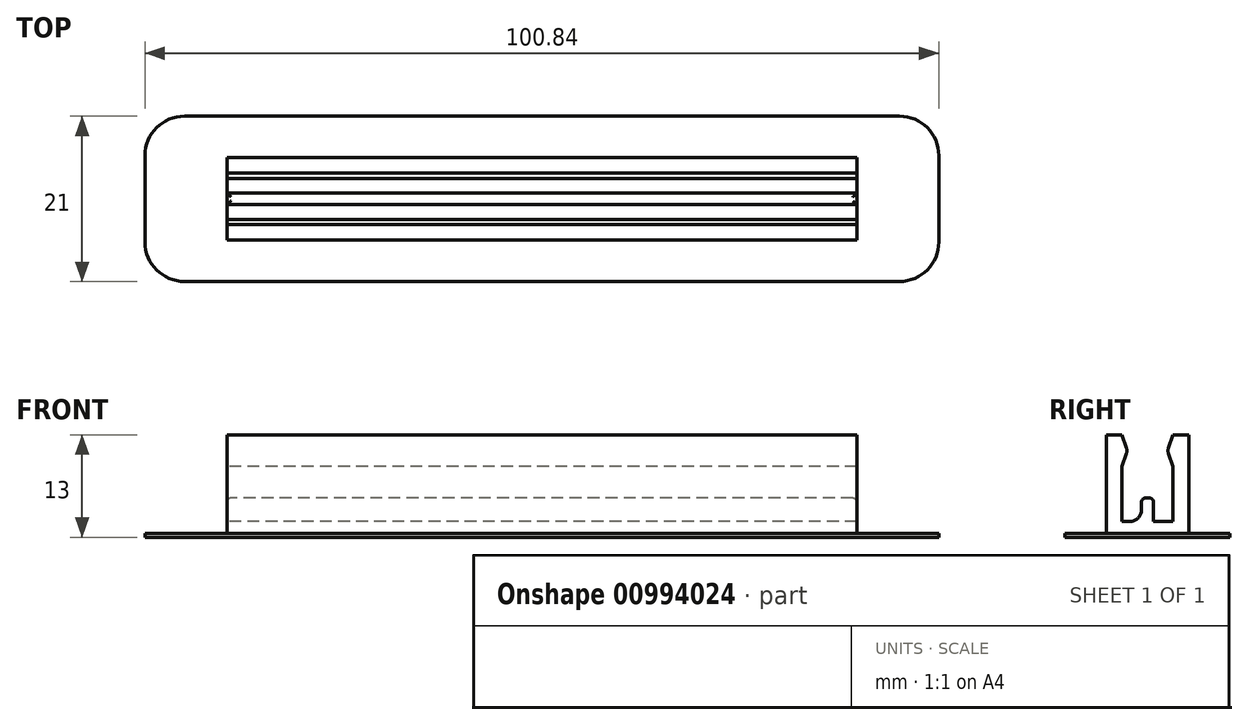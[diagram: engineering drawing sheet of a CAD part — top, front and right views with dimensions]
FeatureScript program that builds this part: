
annotation { "Feature Type Name" : "Feature", "Feature Type Description" : "" }
export const myFeature = defineFeature(function(context is Context, id is Id, definition is map)
    precondition{}
    {
        {
            var Q0;
            Q0=qCreatedBy(makeId("Top.planeOp"),FACE);
            var sketch = newSketch(context, id + "F0", { "sketchPlane" : qUnion([Q0])});
            skLineSegment(sketch, "E0.bottom", {"start": v(40, 5.25) * mm, "end": v(-40, 5.25) * mm});
            skLineSegment(sketch, "E0.top", {"start": v(40, -5.25) * mm, "end": v(-40, -5.25) * mm});
            skLineSegment(sketch, "E0.left", {"start": v(40, 5.25) * mm, "end": v(40, -5.25) * mm});
            skLineSegment(sketch, "E0.right", {"start": v(-40, 5.25) * mm, "end": v(-40, -5.25) * mm});
            skPoint(sketch, "E0.middle", {"position": v(0, 0) * mm});
            skLineSegment(sketch, "E1.bottom", {"start": v(-40, 5.25) * mm, "end": v(40, 5.25) * mm});
            skLineSegment(sketch, "E1.top", {"start": v(-40, 3.25) * mm, "end": v(40, 3.25) * mm});
            skLineSegment(sketch, "E1.left", {"start": v(-40, 5.25) * mm, "end": v(-40, 3.25) * mm});
            skLineSegment(sketch, "E1.right", {"start": v(40, 5.25) * mm, "end": v(40, 3.25) * mm});
            skLineSegment(sketch, "E2.bottom", {"start": v(-40, -5.25) * mm, "end": v(40, -5.25) * mm});
            skLineSegment(sketch, "E2.top", {"start": v(-40, -3.25) * mm, "end": v(40, -3.25) * mm});
            skLineSegment(sketch, "E2.left", {"start": v(-40, -5.25) * mm, "end": v(-40, -3.25) * mm});
            skLineSegment(sketch, "E2.right", {"start": v(40, -5.25) * mm, "end": v(40, -3.25) * mm});
            skLineSegment(sketch, "E3.bottom", {"start": v(45.42, 10.5) * mm, "end": v(-45.42, 10.5) * mm});
            skLineSegment(sketch, "E3.top", {"start": v(45.42, -10.5) * mm, "end": v(-45.42, -10.5) * mm});
            skLineSegment(sketch, "E3.left", {"start": v(50.42, 5.5) * mm, "end": v(50.42, -5.5) * mm});
            skLineSegment(sketch, "E3.right", {"start": v(-50.42, 5.5) * mm, "end": v(-50.42, -5.5) * mm});
            skPoint(sketch, "E4.visualSharp", {"position": v(-50.42, 10.5) * mm});
            skArc(sketch, "E4.filletArc", {"start": v(-45.42, 10.5) * mm, "mid": v(-48.95, 9.03) * mm, "end": v(-50.42, 5.5) * mm});
            skPoint(sketch, "E5.visualSharp", {"position": v(-50.42, -10.5) * mm});
            skArc(sketch, "E5.filletArc", {"start": v(-50.42, -5.5) * mm, "mid": v(-48.95, -9.03) * mm, "end": v(-45.42, -10.5) * mm});
            skPoint(sketch, "E6.visualSharp", {"position": v(50.42, 10.5) * mm});
            skArc(sketch, "E6.filletArc", {"start": v(50.42, 5.5) * mm, "mid": v(48.95, 9.03) * mm, "end": v(45.42, 10.5) * mm});
            skPoint(sketch, "E7.visualSharp", {"position": v(50.42, -10.5) * mm});
            skArc(sketch, "E7.filletArc", {"start": v(45.42, -10.5) * mm, "mid": v(48.95, -9.03) * mm, "end": v(50.42, -5.5) * mm});
            skSolve(sketch);
        }
        {
            var Q0;
            {var subQ0=sQuery(id+"F0.wireOp",EDGE,"E1.top");Q0=makeQuery(id+"F0.imprint","IMPRINT",FACE,{"disambiguationData":[TD([[makeQuery(id+"F0.imprint","IMPRINT",EDGE,{"derivedFrom":subQ0}),-1.0]])]});}
            extrude(context, id + "F1", {"entities" : qUnion([Q0]), "depth" : 2 * mm, "offsetDistance" : 25 * mm});
        }
        {
            var Q0;
            {var subQ0=sQuery(id+"F0.wireOp",EDGE,"E0.bottom");Q0=makeQuery(id+"F0.imprint","IMPRINT",FACE,{"disambiguationData":[TD([[makeQuery(id+"F0.imprint","IMPRINT",EDGE,{"derivedFrom":subQ0}),1.0]])]});}
            var Q1;
            {var subQ0=sQuery(id+"F0.wireOp",EDGE,"E0.top");Q1=makeQuery(id+"F0.imprint","IMPRINT",FACE,{"disambiguationData":[TD([[makeQuery(id+"F0.imprint","IMPRINT",EDGE,{"derivedFrom":subQ0}),-1.0]])]});}
            extrude(context, id + "F2", {"entities" : qUnion([Q0, Q1]), "operationType" : NewBodyOperationType.ADD, "depth" : 13 * mm, "offsetDistance" : 25 * mm});
        }
        {
            var Q0;
            {var subQ0=sQuery(id+"F0.wireOp",EDGE,"E0.right");Q0=makeQuery(id+"F2.boolean.opBoolean","MERGE",FACE,{"derivedFrom":[makeQuery(id+"F1.opExtrude","SWEPT_FACE",FACE,{"disambiguationData":[OSD([subQ0])]}),makeQuery(id+"F2.opExtrude","SWEPT_FACE",FACE,{"disambiguationData":[OSD([subQ0]),TDD([makeQuery(id+"F0.imprint","IMPRINT",EDGE,{"disambiguationData":[TD([[makeQuery(id+"F0.imprint","INTERSECT",VERTEX,{"derivedFrom":[sQuery(id+"F0.wireOp",EDGE,"E0.bottom"),subQ0]}),-1.0]])],"derivedFrom":subQ0})])]}),makeQuery(id+"F2.opExtrude","SWEPT_FACE",FACE,{"disambiguationData":[OSD([subQ0]),TDD([makeQuery(id+"F0.imprint","IMPRINT",EDGE,{"disambiguationData":[TD([[makeQuery(id+"F0.imprint","INTERSECT",VERTEX,{"derivedFrom":[sQuery(id+"F0.wireOp",EDGE,"E0.top"),subQ0]}),1.0]])],"derivedFrom":subQ0})])]})]});}
            var sketch = newSketch(context, id + "F3", { "sketchPlane" : qUnion([Q0])});
            skLineSegment(sketch, "E8.bottom", {"start": v(-5.25, 13) * mm, "end": v(5.25, 13) * mm, "construction": true});
            skLineSegment(sketch, "E8.top", {"start": v(-5.25, 9) * mm, "end": v(5.25, 9) * mm, "construction": true});
            skLineSegment(sketch, "E8.left", {"start": v(-5.25, 13) * mm, "end": v(-5.25, 9) * mm, "construction": true});
            skLineSegment(sketch, "E8.right", {"start": v(5.25, 13) * mm, "end": v(5.25, 9) * mm, "construction": true});
            skLineSegment(sketch, "E9.bottom", {"start": v(-3.25, 13) * mm, "end": v(-2.55, 13) * mm, "construction": true});
            skLineSegment(sketch, "E9.top", {"start": v(-3.25, 9) * mm, "end": v(-2.55, 9) * mm, "construction": true});
            skLineSegment(sketch, "E9.left", {"start": v(-3.25, 13) * mm, "end": v(-3.25, 9) * mm, "construction": true});
            skLineSegment(sketch, "E9.right", {"start": v(-2.55, 13) * mm, "end": v(-2.55, 9) * mm, "construction": true});
            skLineSegment(sketch, "E10.top", {"start": v(3.25, 13) * mm, "end": v(3.05, 13) * mm, "construction": true});
            skLineSegment(sketch, "E10.left", {"start": v(3.25, 7.5) * mm, "end": v(3.25, 13) * mm, "construction": true});
            skLineSegment(sketch, "E11.bottom", {"start": v(-3.25, 13) * mm, "end": v(3.25, 13) * mm, "construction": true});
            skLineSegment(sketch, "E11.left", {"start": v(-3.25, 13) * mm, "end": v(-3.25, 10.25) * mm, "construction": true});
            skLineSegment(sketch, "E11.right", {"start": v(3.25, 13) * mm, "end": v(3.25, 10.25) * mm, "construction": true});
            skLineSegment(sketch, "E12", {"start": v(-3.25, 9) * mm, "end": v(-2.55, 11) * mm});
            skLineSegment(sketch, "E13", {"start": v(-2.55, 11) * mm, "end": v(-3.25, 13) * mm});
            skLineSegment(sketch, "E14.top", {"start": v(-3.25, 11) * mm, "end": v(3.25, 11) * mm, "construction": true});
            skLineSegment(sketch, "E14.left", {"start": v(-3.25, 13) * mm, "end": v(-3.25, 11) * mm, "construction": true});
            skLineSegment(sketch, "E14.right", {"start": v(3.25, 13) * mm, "end": v(3.25, 11) * mm, "construction": true});
            skLineSegment(sketch, "E15.bottom", {"start": v(3.25, 13) * mm, "end": v(2.55, 13) * mm, "construction": true});
            skLineSegment(sketch, "E15.top", {"start": v(3.25, 9) * mm, "end": v(2.55, 9) * mm, "construction": true});
            skLineSegment(sketch, "E15.left", {"start": v(3.25, 13) * mm, "end": v(3.25, 9) * mm, "construction": true});
            skLineSegment(sketch, "E15.right", {"start": v(2.55, 13) * mm, "end": v(2.55, 9) * mm, "construction": true});
            skLineSegment(sketch, "E16", {"start": v(3.25, 9) * mm, "end": v(2.55, 11) * mm});
            skLineSegment(sketch, "E17", {"start": v(2.55, 11) * mm, "end": v(3.25, 13) * mm});
            skLineSegment(sketch, "E18.bottom", {"start": v(-0.75, 2) * mm, "end": v(0.75, 2) * mm});
            skLineSegment(sketch, "E18.top", {"start": v(-0.75, 5) * mm, "end": v(0.75, 5) * mm});
            skLineSegment(sketch, "E18.left", {"start": v(-0.75, 2) * mm, "end": v(-0.75, 5) * mm});
            skLineSegment(sketch, "E18.right", {"start": v(0.75, 2) * mm, "end": v(0.75, 5) * mm});
            skSolve(sketch);
        }
        {
            var Q0;
            {var subQ0=sQuery(id+"F3.wireOp",EDGE,"E12");Q0=makeQuery(id+"F3.imprint","IMPRINT",FACE,{"disambiguationData":[TD([[makeQuery(id+"F3.imprint","IMPRINT",EDGE,{"derivedFrom":subQ0}),1.0]])]});}
            var Q1;
            {var subQ0=sQuery(id+"F3.wireOp",EDGE,"JF0y7yOE-hZ0c-IGpq-qxWO-KcFmzZiD7cJA");Q1=makeQuery(id+"F3.imprint","IMPRINT",FACE,{"disambiguationData":[TD([[makeQuery(id+"F3.imprint","IMPRINT",EDGE,{"derivedFrom":subQ0}),-1.0]])]});}
            var Q2;
            {var subQ0=sQuery(id+"F3.wireOp",EDGE,"E16");Q2=makeQuery(id+"F3.imprint","IMPRINT",FACE,{"disambiguationData":[TD([[makeQuery(id+"F3.imprint","IMPRINT",EDGE,{"derivedFrom":subQ0}),-1.0]])]});}
            var Q3;
            Q3=makeQuery(id+"F3.imprint","IMPRINT",FACE,{"disambiguationData":[TD([[makeQuery(id+"F3.imprint","IMPRINT",EDGE,{"derivedFrom":sQuery(id+"F3.wireOp",EDGE,"E18.bottom")}),1.0]])]});
            extrude(context, id + "F4", {"entities" : qUnion([Q0, Q1, Q2, Q3]), "operationType" : NewBodyOperationType.ADD, "depth" : -80 * mm, "offsetDistance" : 25 * mm});
        }
        {
            var Q0;
            Q0=makeQuery(id+"F4.opExtrude","SWEPT_EDGE",EDGE,{"disambiguationData":[OSD([sQuery(id+"F3.wireOp",EDGE,"E12"),sQuery(id+"F3.wireOp",EDGE,"E13")])]});
            fillet(context, id + "F5", {"entities" : qUnion([Q0]), "radius" : 1 * mm, "tangentPropagation" : true, "allowEdgeOverflow" : false});
        }
        {
            var Q0;
            Q0=makeQuery(id+"F4.opExtrude","SWEPT_EDGE",EDGE,{"disambiguationData":[OSD([sQuery(id+"F3.wireOp",EDGE,"E16"),sQuery(id+"F3.wireOp",EDGE,"E17")])]});
            fillet(context, id + "F6", {"entities" : qUnion([Q0]), "radius" : 1 * mm, "tangentPropagation" : true, "allowEdgeOverflow" : false});
        }
        {
            var Q0;
            Q0=makeQuery(id+"F1.opExtrude","CAP_EDGE",EDGE,{"disambiguationData":[OSD([sQuery(id+"F0.wireOp",EDGE,"E2.top")])],"isStart":false});
            var Q1;
            Q1=makeQuery(id+"F1.opExtrude","CAP_EDGE",EDGE,{"disambiguationData":[OSD([sQuery(id+"F0.wireOp",EDGE,"E1.top")])],"isStart":false});
            var Q2;
            Q2=makeQuery(id+"F4.opExtrude","SWEPT_EDGE",EDGE,{"disambiguationData":[OSD([sQuery(id+"F0.wireOp",EDGE,"E0.right"),sQuery(id+"F3.wireOp",EDGE,"E18.bottom"),sQuery(id+"F3.wireOp",EDGE,"E18.right")])]});
            var Q3;
            Q3=makeQuery(id+"F4.opExtrude","SWEPT_EDGE",EDGE,{"disambiguationData":[OSD([sQuery(id+"F0.wireOp",EDGE,"E0.right"),sQuery(id+"F3.wireOp",EDGE,"E18.bottom"),sQuery(id+"F3.wireOp",EDGE,"E18.left")])]});
            fillet(context, id + "F7", {"entities" : qUnion([Q0, Q1, Q2, Q3]), "radius" : 1.5 * mm, "tangentPropagation" : true, "allowEdgeOverflow" : false});
        }
        {
            var Q0;
            Q0=makeQuery(id+"F4.opExtrude","SWEPT_FACE",FACE,{"disambiguationData":[OSD([sQuery(id+"F3.wireOp",EDGE,"E18.top")])]});
            var Q1;
            Q1=makeQuery(id+"F4.opExtrude","SWEPT_EDGE",EDGE,{"disambiguationData":[OSD([sQuery(id+"F3.wireOp",EDGE,"E18.top"),sQuery(id+"F3.wireOp",EDGE,"E18.left")])]});
            fillet(context, id + "F8", {"entities" : qUnion([Q0, Q1]), "radius" : 0.5 * mm, "tangentPropagation" : true, "allowEdgeOverflow" : false});
        }
        {
            var Q0;
            {var subQ4=sQuery(id+"F0.wireOp",EDGE,"E0.bottom");Q0=makeQuery(id+"F0.imprint","IMPRINT",FACE,{"disambiguationData":[TD([[makeQuery(id+"F0.imprint","IMPRINT",EDGE,{"derivedFrom":subQ4}),-1.0]])]});}
            extrude(context, id + "F9", {"entities" : qUnion([Q0]), "operationType" : NewBodyOperationType.ADD, "depth" : 0.5 * mm, "offsetDistance" : 25 * mm});
        }
    });
